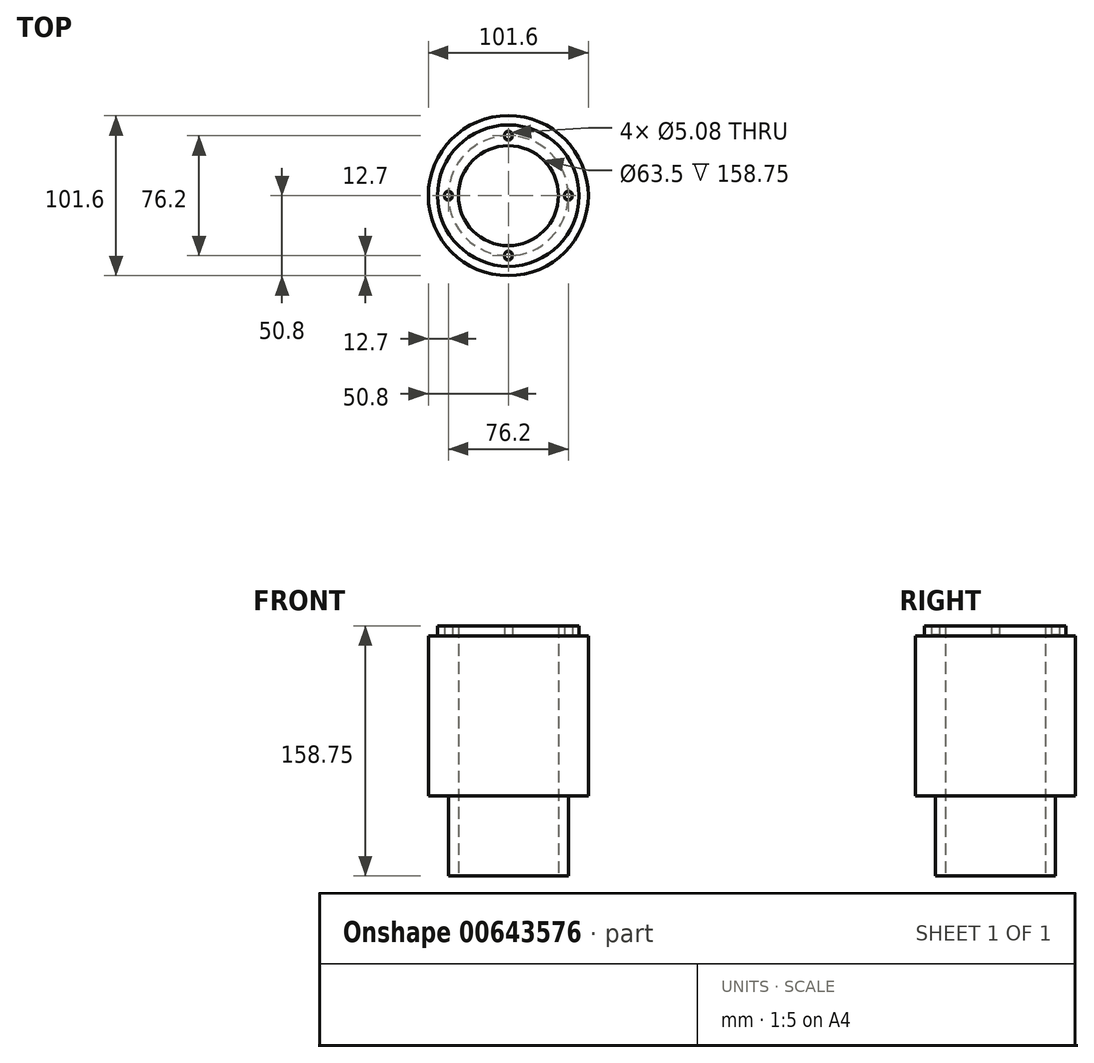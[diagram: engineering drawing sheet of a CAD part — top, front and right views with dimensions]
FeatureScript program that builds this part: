
annotation { "Feature Type Name" : "Feature", "Feature Type Description" : "" }
export const myFeature = defineFeature(function(context is Context, id is Id, definition is map)
    precondition{}
    {
        {
            var Q0;
            Q0=qCreatedBy(makeId("Top.planeOp"),FACE);
            var sketch = newSketch(context, id + "F0", { "sketchPlane" : qUnion([Q0])});
            skCircle(sketch, "E0", {"center": v(0, 0) * mm, "radius": 50.8 * mm});
            skSolve(sketch);
        }
        {
            var Q0;
            Q0 = qSketchRegion(id + "F0", true);
            extrude(context, id + "F1", {"entities" : qUnion([Q0]), "depth" : 101.6 * mm, "offsetDistance" : 25.4 * mm});
        }
        {
            var Q0;
            Q0=makeQuery(id+"F1.opExtrude","CAP_FACE",FACE,{"disambiguationData":[OSD([sQuery(id+"F0.wireOp",EDGE,"E0")])],"isStart":true});
            var sketch = newSketch(context, id + "F2", { "sketchPlane" : qUnion([Q0])});
            skCircle(sketch, "E1", {"center": v(0, 0) * mm, "radius": 38.1 * mm});
            skSolve(sketch);
        }
        {
            var Q0;
            Q0 = qSketchRegion(id + "F2", true);
            extrude(context, id + "F3", {"entities" : qUnion([Q0]), "operationType" : NewBodyOperationType.ADD, "depth" : 50.8 * mm, "offsetDistance" : 25.4 * mm});
        }
        {
            var Q0;
            Q0=makeQuery(id+"F3.opExtrude","CAP_FACE",FACE,{"disambiguationData":[OSD([sQuery(id+"F2.wireOp",EDGE,"E1")])],"isStart":false});
            var sketch = newSketch(context, id + "F4", { "sketchPlane" : qUnion([Q0])});
            skCircle(sketch, "E2", {"center": v(0, 0) * mm, "radius": 31.75 * mm});
            skSolve(sketch);
        }
        {
            var Q0;
            Q0=makeQuery(id+"F4.imprint","IMPRINT",FACE,{"disambiguationData":[TD([[makeQuery(id+"F4.imprint","IMPRINT",EDGE,{"derivedFrom":sQuery(id+"F4.wireOp",EDGE,"E2")}),1.0]])]});
            extrude(context, id + "F5", {"entities" : qUnion([Q0]), "operationType" : NewBodyOperationType.REMOVE, "oppositeDirection" : true, "depth" : 152.4 * mm, "offsetDistance" : 25.4 * mm});
        }
        {
            var Q0;
            Q0=makeQuery(id+"F1.opExtrude","CAP_FACE",FACE,{"disambiguationData":[OSD([sQuery(id+"F0.wireOp",EDGE,"E0")])],"isStart":false});
            var sketch = newSketch(context, id + "F6", { "sketchPlane" : qUnion([Q0])});
            skPoint(sketch, "E3", {"position": v(0, 38.1) * mm});
            skPoint(sketch, "E4", {"position": v(38.1, 0) * mm});
            skPoint(sketch, "E5", {"position": v(-38.1, 0) * mm});
            skPoint(sketch, "E6", {"position": v(0, -38.1) * mm});
            skSolve(sketch);
        }
        {
            var Q0;
            Q0=makeQuery(id+"F1.opExtrude","CAP_FACE",FACE,{"disambiguationData":[OSD([sQuery(id+"F0.wireOp",EDGE,"E0")])],"isStart":false});
            var sketch = newSketch(context, id + "F7", { "sketchPlane" : qUnion([Q0])});
            skCircle(sketch, "E7", {"center": v(0, 0) * mm, "radius": 44.91 * mm});
            skSolve(sketch);
        }
        {
            var Q0;
            Q0=makeQuery(id+"F7.imprint","IMPRINT",FACE,{"disambiguationData":[TD([[makeQuery(id+"F7.imprint","IMPRINT",EDGE,{"derivedFrom":makeQuery(id+"F5.boolean.opBoolean","COPY",EDGE,{"derivedFrom":makeQuery(id+"F5.opExtrude","CAP_EDGE",EDGE,{"disambiguationData":[OSD([sQuery(id+"F4.wireOp",EDGE,"E2")])],"isStart":false})})}),-1.0]])]});
            var Q1;
            Q1=makeQuery(id+"F7.imprint","IMPRINT",FACE,{"disambiguationData":[TD([[makeQuery(id+"F7.imprint","IMPRINT",EDGE,{"derivedFrom":makeQuery(id+"F8dVB6ojBn8Ljg2_1.hole-0.boolean.opBoolean","COPY",EDGE,{"derivedFrom":makeQuery(id+"F8dVB6ojBn8Ljg2_1.hole-0.opRevolve","SWEPT_EDGE",EDGE,{"disambiguationData":[OSD([sQuery(id+"F8dVB6ojBn8Ljg2_1.hole-0.sketch.wireOp",EDGE,"csink_start_line_1"),sQuery(id+"F8dVB6ojBn8Ljg2_1.hole-0.sketch.wireOp",EDGE,"csink_start_line_2")])]})})}),1.0]])]});
            var Q2;
            Q2=makeQuery(id+"F7.imprint","IMPRINT",FACE,{"disambiguationData":[TD([[makeQuery(id+"F7.imprint","IMPRINT",EDGE,{"derivedFrom":makeQuery(id+"F8dVB6ojBn8Ljg2_1.hole-1.boolean.opBoolean","COPY",EDGE,{"derivedFrom":makeQuery(id+"F8dVB6ojBn8Ljg2_1.hole-1.opRevolve","SWEPT_EDGE",EDGE,{"disambiguationData":[OSD([sQuery(id+"F8dVB6ojBn8Ljg2_1.hole-1.sketch.wireOp",EDGE,"csink_start_line_1"),sQuery(id+"F8dVB6ojBn8Ljg2_1.hole-1.sketch.wireOp",EDGE,"csink_start_line_2")])]})})}),1.0]])]});
            var Q3;
            Q3=makeQuery(id+"F7.imprint","IMPRINT",FACE,{"disambiguationData":[TD([[makeQuery(id+"F7.imprint","IMPRINT",EDGE,{"derivedFrom":makeQuery(id+"F8dVB6ojBn8Ljg2_1.hole-2.boolean.opBoolean","COPY",EDGE,{"derivedFrom":makeQuery(id+"F8dVB6ojBn8Ljg2_1.hole-2.opRevolve","SWEPT_EDGE",EDGE,{"disambiguationData":[OSD([sQuery(id+"F8dVB6ojBn8Ljg2_1.hole-2.sketch.wireOp",EDGE,"csink_start_line_1"),sQuery(id+"F8dVB6ojBn8Ljg2_1.hole-2.sketch.wireOp",EDGE,"csink_start_line_2")])]})})}),1.0]])]});
            var Q4;
            Q4=makeQuery(id+"F7.imprint","IMPRINT",FACE,{"disambiguationData":[TD([[makeQuery(id+"F7.imprint","IMPRINT",EDGE,{"derivedFrom":makeQuery(id+"F8dVB6ojBn8Ljg2_1.hole-3.boolean.opBoolean","COPY",EDGE,{"derivedFrom":makeQuery(id+"F8dVB6ojBn8Ljg2_1.hole-3.opRevolve","SWEPT_EDGE",EDGE,{"disambiguationData":[OSD([sQuery(id+"F8dVB6ojBn8Ljg2_1.hole-3.sketch.wireOp",EDGE,"csink_start_line_1"),sQuery(id+"F8dVB6ojBn8Ljg2_1.hole-3.sketch.wireOp",EDGE,"csink_start_line_2")])]})})}),1.0]])]});
            var Q5;
            Q5=makeQuery(id+"F7.imprint","IMPRINT",FACE,{"disambiguationData":[TD([[makeQuery(id+"F7.imprint","IMPRINT",EDGE,{"derivedFrom":sQuery(id+"F7.wireOp",EDGE,"E7")}),1.0]])]});
            extrude(context, id + "F8", {"entities" : qUnion([Q0, Q1, Q2, Q3, Q4, Q5]), "operationType" : NewBodyOperationType.ADD, "depth" : 6.35 * mm, "offsetDistance" : 25.4 * mm});
        }
        {
            var Q0;
            Q0=sQuery(id+"F6.wireOp",VERTEX,"E3");
            var Q1;
            Q1=sQuery(id+"F6.wireOp",VERTEX,"E4");
            var Q2;
            Q2=sQuery(id+"F6.wireOp",VERTEX,"E6");
            var Q3;
            Q3=sQuery(id+"F6.wireOp",VERTEX,"E5");
            var Q4;
            Q4=makeQuery(id+"F1.opExtrude","SWEPT_BODY",BODY,{"disambiguationData":[OSD([sQuery(id+"F0.wireOp",EDGE,"E0")])]});
            hole(context, id + "F9", {"style" : HoleStyle.C_SINK, "endStyle" : HoleEndStyle.THROUGH, "oppositeDirection" : true, "holeDiameter" : 5.08 * mm, "cSinkDiameter" : 6.48 * mm, "cSinkAngle" : 85 * degree, "majorDiameter" : 2.84 * mm, "tappedDepth" : 10.8 * mm, "tapClearance" : 3, "startFromSketch" : true, "locations" : qUnion([Q0, Q1, Q2, Q3]), "scope" : qUnion([Q4])});
        }
    });
